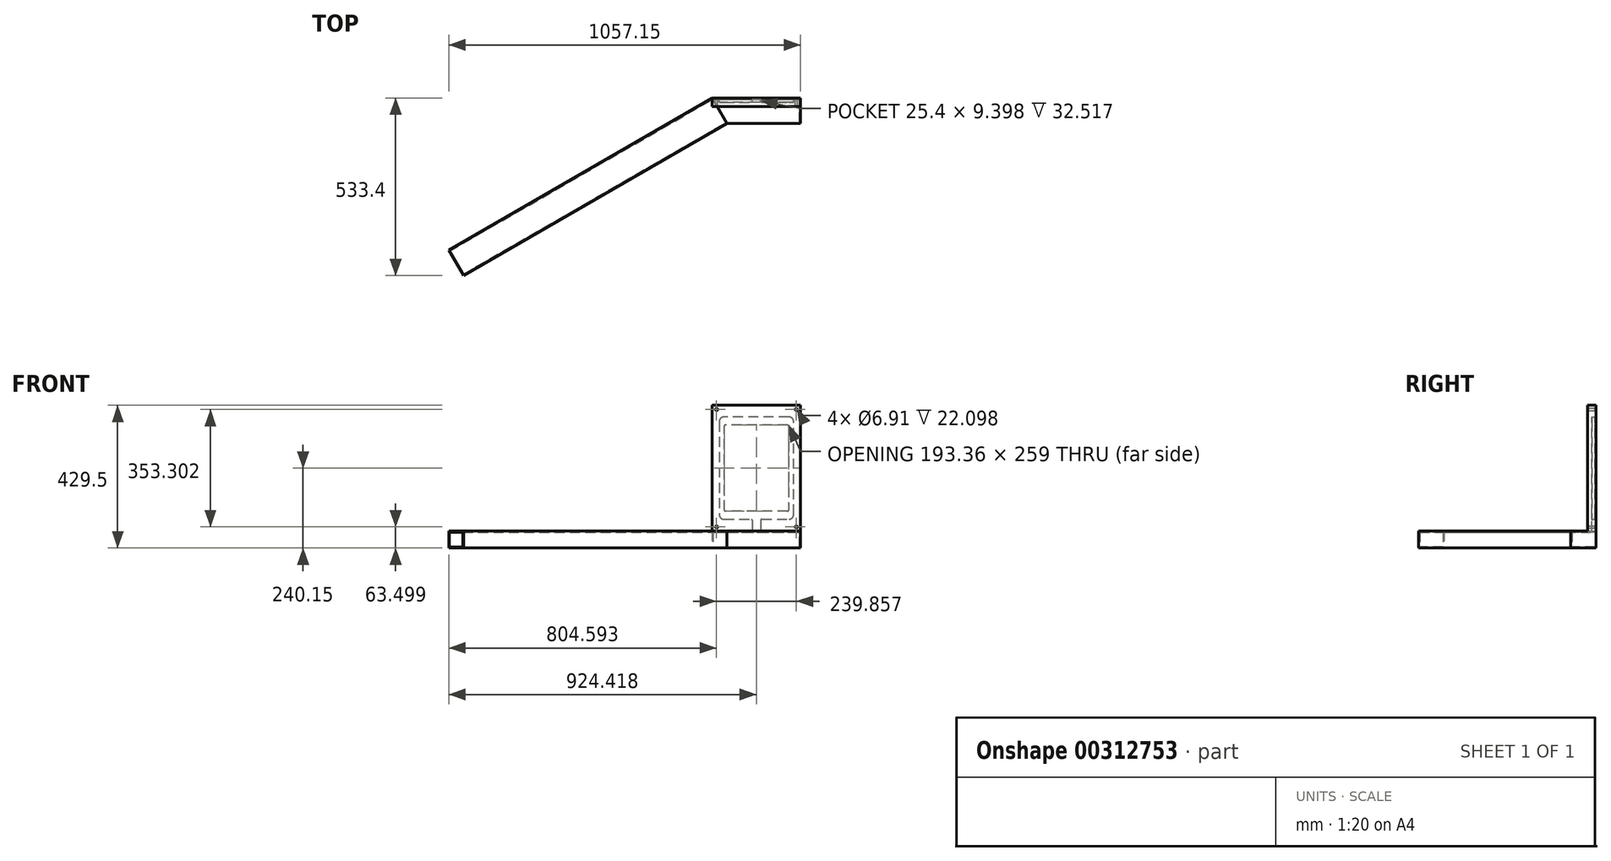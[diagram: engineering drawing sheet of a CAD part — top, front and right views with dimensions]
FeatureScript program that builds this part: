
annotation { "Feature Type Name" : "Feature", "Feature Type Description" : "" }
export const myFeature = defineFeature(function(context is Context, id is Id, definition is map)
    precondition{}
    {
        {
            var Q0;
            Q0=qCreatedBy(makeId("Front.planeOp"),FACE);
            var sketch = newSketch(context, id + "F0", { "sketchPlane" : qUnion([Q0])});
            skLineSegment(sketch, "E0", {"start": v(-259.8, 139.98) * mm, "end": v(-259.82, -139.5) * mm});
            skArc(sketch, "E1", {"start": v(-259.82, -139.5) * mm, "mid": v(-255.63, -149.6) * mm, "end": v(-245.53, -153.79) * mm});
            skLineSegment(sketch, "E2", {"start": v(-245.53, -153.79) * mm, "end": v(-163.8, -153.79) * mm});
            skArc(sketch, "E3", {"start": v(-160.76, -156.83) * mm, "mid": v(-161.65, -154.68) * mm, "end": v(-163.8, -153.79) * mm});
            skLineSegment(sketch, "E4", {"start": v(-160.76, -156.83) * mm, "end": v(-160.76, -171.77) * mm});
            skArc(sketch, "E5", {"start": v(-132.3, -153.79) * mm, "mid": v(-134.46, -154.68) * mm, "end": v(-135.36, -156.83) * mm});
            skLineSegment(sketch, "E6", {"start": v(-132.3, -153.79) * mm, "end": v(-50.58, -153.79) * mm});
            skArc(sketch, "E7", {"start": v(-50.58, -153.79) * mm, "mid": v(-40.48, -149.6) * mm, "end": v(-36.3, -139.5) * mm});
            skLineSegment(sketch, "E8", {"start": v(-36.3, -139.5) * mm, "end": v(-36.29, 139.97) * mm});
            skArc(sketch, "E9", {"start": v(-36.29, 139.97) * mm, "mid": v(-40.47, 150.08) * mm, "end": v(-50.58, 154.26) * mm});
            skLineSegment(sketch, "E10", {"start": v(-50.58, 154.26) * mm, "end": v(-245.52, 154.26) * mm});
            skArc(sketch, "E11", {"start": v(-245.52, 154.26) * mm, "mid": v(-255.63, 150.08) * mm, "end": v(-259.8, 139.98) * mm});
            skLineSegment(sketch, "E12", {"start": v(-244.82, -126.32) * mm, "end": v(-244.82, 126.32) * mm});
            skLineSegment(sketch, "E13", {"start": v(-54.64, -129.5) * mm, "end": v(-241.65, -129.5) * mm});
            skArc(sketch, "E14", {"start": v(-241.65, 129.5) * mm, "mid": v(-243.9, 128.57) * mm, "end": v(-244.82, 126.32) * mm});
            skArc(sketch, "E15", {"start": v(-51.46, 126.32) * mm, "mid": v(-52.4, 128.57) * mm, "end": v(-54.64, 129.5) * mm});
            skArc(sketch, "E16", {"start": v(-244.82, -126.32) * mm, "mid": v(-243.9, -128.57) * mm, "end": v(-241.65, -129.5) * mm});
            skArc(sketch, "E17", {"start": v(-54.64, -129.5) * mm, "mid": v(-52.4, -128.57) * mm, "end": v(-51.46, -126.32) * mm});
            skLineSegment(sketch, "E18", {"start": v(-135.36, -171.77) * mm, "end": v(-135.36, -156.83) * mm});
            skLineSegment(sketch, "E19", {"start": v(-160.76, -171.77) * mm, "end": v(-160.76, -187.92) * mm});
            skLineSegment(sketch, "E20", {"start": v(-135.36, -171.77) * mm, "end": v(-135.36, -187.92) * mm});
            skLineSegment(sketch, "E21", {"start": v(-160.76, -187.92) * mm, "end": v(-160.76, -189.35) * mm});
            skLineSegment(sketch, "E22", {"start": v(-135.36, -187.92) * mm, "end": v(-135.36, -189.35) * mm});
            skLineSegment(sketch, "E23", {"start": v(-15.41, -189.35) * mm, "end": v(-15.41, 189.35) * mm});
            skLineSegment(sketch, "E24", {"start": v(-280.67, -189.35) * mm, "end": v(-280.67, 189.35) * mm});
            skLineSegment(sketch, "E25", {"start": v(-15.41, 189.35) * mm, "end": v(-280.67, 189.35) * mm});
            skLineSegment(sketch, "E26", {"start": v(-280.67, -189.35) * mm, "end": v(-15.41, -189.35) * mm});
            skArc(sketch, "E27", {"start": v(-264.51, -176.65) * mm, "mid": v(-267.97, -173.2) * mm, "end": v(-271.42, -176.65) * mm});
            skArc(sketch, "E28", {"start": v(-271.42, -176.65) * mm, "mid": v(-267.97, -180.1) * mm, "end": v(-264.51, -176.65) * mm});
            skArc(sketch, "E29", {"start": v(-24.66, -176.65) * mm, "mid": v(-28.11, -173.2) * mm, "end": v(-31.56, -176.65) * mm});
            skArc(sketch, "E30", {"start": v(-31.56, -176.65) * mm, "mid": v(-28.11, -180.1) * mm, "end": v(-24.66, -176.65) * mm});
            skArc(sketch, "E31", {"start": v(-24.66, 176.65) * mm, "mid": v(-28.11, 180.1) * mm, "end": v(-31.56, 176.65) * mm});
            skArc(sketch, "E32", {"start": v(-31.56, 176.65) * mm, "mid": v(-28.11, 173.2) * mm, "end": v(-24.66, 176.65) * mm});
            skArc(sketch, "E33", {"start": v(-264.51, 176.65) * mm, "mid": v(-267.97, 180.1) * mm, "end": v(-271.42, 176.65) * mm});
            skArc(sketch, "E34", {"start": v(-271.42, 176.65) * mm, "mid": v(-267.97, 173.2) * mm, "end": v(-264.51, 176.65) * mm});
            skLineSegment(sketch, "E35", {"start": v(-54.64, 129.5) * mm, "end": v(-241.65, 129.5) * mm});
            skLineSegment(sketch, "E36", {"start": v(-51.46, 126.32) * mm, "end": v(-51.46, -126.32) * mm});
            skLineSegment(sketch, "E37", {"start": v(280.67, -189.35) * mm, "end": v(280.67, 189.35) * mm});
            skLineSegment(sketch, "E38", {"start": v(15.41, -189.35) * mm, "end": v(15.41, 189.35) * mm});
            skLineSegment(sketch, "E39", {"start": v(280.67, 189.35) * mm, "end": v(15.41, 189.35) * mm});
            skLineSegment(sketch, "E40", {"start": v(15.41, -189.35) * mm, "end": v(280.67, -189.35) * mm});
            skArc(sketch, "E41", {"start": v(31.56, -176.65) * mm, "mid": v(28.11, -173.2) * mm, "end": v(24.66, -176.65) * mm});
            skArc(sketch, "E42", {"start": v(24.66, -176.65) * mm, "mid": v(28.11, -180.1) * mm, "end": v(31.56, -176.65) * mm});
            skArc(sketch, "E43", {"start": v(271.42, -176.65) * mm, "mid": v(267.97, -173.2) * mm, "end": v(264.51, -176.65) * mm});
            skArc(sketch, "E44", {"start": v(264.51, -176.65) * mm, "mid": v(267.97, -180.1) * mm, "end": v(271.42, -176.65) * mm});
            skArc(sketch, "E45", {"start": v(271.42, 176.65) * mm, "mid": v(267.97, 180.1) * mm, "end": v(264.51, 176.65) * mm});
            skArc(sketch, "E46", {"start": v(264.51, 176.65) * mm, "mid": v(267.97, 173.2) * mm, "end": v(271.42, 176.65) * mm});
            skArc(sketch, "E47", {"start": v(31.56, 176.65) * mm, "mid": v(28.11, 180.1) * mm, "end": v(24.66, 176.65) * mm});
            skArc(sketch, "E48", {"start": v(24.66, 176.65) * mm, "mid": v(28.11, 173.2) * mm, "end": v(31.56, 176.65) * mm});
            skSolve(sketch);
        }
        {
            var Q0;
            Q0=makeQuery(id+"F0.imprint","IMPRINT",FACE,{"disambiguationData":[TD([[makeQuery(id+"F0.imprint","IMPRINT",EDGE,{"derivedFrom":sQuery(id+"F0.wireOp",EDGE,"E37")}),1.0]])]});
            var Q1;
            Q1=makeQuery(id+"F0.imprint","IMPRINT",FACE,{"disambiguationData":[TD([[makeQuery(id+"F0.imprint","IMPRINT",EDGE,{"derivedFrom":sQuery(id+"F0.wireOp",EDGE,"E0")}),-1.0]])]});
            extrude(context, id + "F1", {"entities" : qUnion([Q0, Q1]), "depth" : 12.7 * mm});
        }
        {
            var Q0;
            Q0=makeQuery(id+"F0.imprint","IMPRINT",FACE,{"disambiguationData":[TD([[makeQuery(id+"F0.imprint","IMPRINT",EDGE,{"derivedFrom":sQuery(id+"F0.wireOp",EDGE,"E0")}),1.0]])]});
            var Q1;
            Q1=makeQuery(id+"F0.imprint","IMPRINT",FACE,{"disambiguationData":[TD([[makeQuery(id+"F0.imprint","IMPRINT",EDGE,{"derivedFrom":sQuery(id+"F0.wireOp",EDGE,"E31")}),1.0]])]});
            var Q2;
            Q2=makeQuery(id+"F0.imprint","IMPRINT",FACE,{"disambiguationData":[TD([[makeQuery(id+"F0.imprint","IMPRINT",EDGE,{"derivedFrom":sQuery(id+"F0.wireOp",EDGE,"E29")}),1.0]])]});
            var Q3;
            Q3=makeQuery(id+"F0.imprint","IMPRINT",FACE,{"disambiguationData":[TD([[makeQuery(id+"F0.imprint","IMPRINT",EDGE,{"derivedFrom":sQuery(id+"F0.wireOp",EDGE,"E27")}),1.0]])]});
            var Q4;
            Q4=makeQuery(id+"F0.imprint","IMPRINT",FACE,{"disambiguationData":[TD([[makeQuery(id+"F0.imprint","IMPRINT",EDGE,{"derivedFrom":sQuery(id+"F0.wireOp",EDGE,"E33")}),1.0]])]});
            extrude(context, id + "F2", {"entities" : qUnion([Q0, Q1, Q2, Q3, Q4]), "operationType" : NewBodyOperationType.ADD, "depth" : 3.3 * mm});
        }
        {
            var Q0;
            Q0=makeQuery(id+"F1.opExtrude","SWEPT_FACE",FACE,{"disambiguationData":[OSD([sQuery(id+"F0.wireOp",EDGE,"E23")])]});
            var sketch = newSketch(context, id + "F3", { "sketchPlane" : qUnion([Q0])});
            skLineSegment(sketch, "E49.bottom", {"start": v(0, -189.35) * mm, "end": v(-76.2, -189.35) * mm});
            skLineSegment(sketch, "E49.top", {"start": v(0, -240.15) * mm, "end": v(-76.2, -240.15) * mm});
            skLineSegment(sketch, "E49.left", {"start": v(0, -189.35) * mm, "end": v(0, -240.15) * mm});
            skLineSegment(sketch, "E49.right", {"start": v(-76.2, -189.35) * mm, "end": v(-76.2, -240.15) * mm});
            skLineSegment(sketch, "E50.0", {"start": v(-3.17, -236.98) * mm, "end": v(-73.02, -236.98) * mm});
            skLineSegment(sketch, "E50.1", {"start": v(-3.18, -192.53) * mm, "end": v(-3.17, -236.98) * mm});
            skLineSegment(sketch, "E50.2", {"start": v(-3.18, -192.53) * mm, "end": v(-73.02, -192.53) * mm});
            skLineSegment(sketch, "E50.3", {"start": v(-73.02, -192.53) * mm, "end": v(-73.02, -236.98) * mm});
            skSolve(sketch);
        }
        {
            var Q0;
            Q0 = qSketchRegion(id + "F3", true);
            var Q1;
            Q1=makeQuery(id+"F1.opExtrude","SWEPT_FACE",FACE,{"disambiguationData":[OSD([sQuery(id+"F0.wireOp",EDGE,"E24")])]});
            extrude(context, id + "F4", {"entities" : qUnion([Q0]), "endBound" : BoundingType.UP_TO_SURFACE, "oppositeDirection" : true, "endBoundEntityFace" : qUnion([Q1]), "depth" : 275.59 * mm});
        }
        {
            var Q0;
            Q0=makeQuery(id+"F4.opExtrude","SWEPT_FACE",FACE,{"disambiguationData":[OSD([sQuery(id+"F3.wireOp",EDGE,"E49.top")])]});
            var sketch = newSketch(context, id + "F5", { "sketchPlane" : qUnion([Q0])});
            skLineSegment(sketch, "E51", {"start": v(-280.67, 0) * mm, "end": v(-280.67, 76.2) * mm});
            skLineSegment(sketch, "E52", {"start": v(-280.67, 76.2) * mm, "end": v(-236.67, 76.2) * mm});
            skLineSegment(sketch, "E53", {"start": v(-236.67, 76.2) * mm, "end": v(-280.67, 0) * mm});
            skSolve(sketch);
        }
        {
            var Q0;
            Q0=makeQuery(id+"F5.imprint","IMPRINT",FACE,{"disambiguationData":[TD([[makeQuery(id+"F5.imprint","IMPRINT",EDGE,{"derivedFrom":sQuery(id+"F5.wireOp",EDGE,"E51")}),-1.0]])]});
            extrude(context, id + "F6", {"entities" : qUnion([Q0]), "operationType" : NewBodyOperationType.REMOVE, "oppositeDirection" : true, "depth" : 50.8 * mm});
        }
        {
            var Q0;
            Q0=makeQuery(id+"F6.boolean.opBoolean","COPY",FACE,{"derivedFrom":makeQuery(id+"F6.opExtrude","SWEPT_FACE",FACE,{"disambiguationData":[OSD([sQuery(id+"F5.wireOp",EDGE,"E53")])]})});
            extrude(context, id + "F7", {"entities" : qUnion([Q0]), "depth" : 914.4 * mm});
        }
        {
            var Q0;
            Q0=makeQuery(id+"F1.opExtrude","CAP_FACE",FACE,{"disambiguationData":[OSD([sQuery(id+"F0.wireOp",EDGE,"E0"),sQuery(id+"F0.wireOp",EDGE,"E1"),sQuery(id+"F0.wireOp",EDGE,"E2"),sQuery(id+"F0.wireOp",EDGE,"E3"),sQuery(id+"F0.wireOp",EDGE,"E4"),sQuery(id+"F0.wireOp",EDGE,"E5"),sQuery(id+"F0.wireOp",EDGE,"E6"),sQuery(id+"F0.wireOp",EDGE,"E7"),sQuery(id+"F0.wireOp",EDGE,"E8"),sQuery(id+"F0.wireOp",EDGE,"E9"),sQuery(id+"F0.wireOp",EDGE,"E10"),sQuery(id+"F0.wireOp",EDGE,"E11"),sQuery(id+"F0.wireOp",EDGE,"E18"),sQuery(id+"F0.wireOp",EDGE,"E19"),sQuery(id+"F0.wireOp",EDGE,"E20"),sQuery(id+"F0.wireOp",EDGE,"E21"),sQuery(id+"F0.wireOp",EDGE,"E22"),sQuery(id+"F0.wireOp",EDGE,"E23"),sQuery(id+"F0.wireOp",EDGE,"E24"),sQuery(id+"F0.wireOp",EDGE,"E25"),sQuery(id+"F0.wireOp",EDGE,"E26"),sQuery(id+"F0.wireOp",EDGE,"E27"),sQuery(id+"F0.wireOp",EDGE,"E28"),sQuery(id+"F0.wireOp",EDGE,"E29"),sQuery(id+"F0.wireOp",EDGE,"E30"),sQuery(id+"F0.wireOp",EDGE,"E31"),sQuery(id+"F0.wireOp",EDGE,"E32"),sQuery(id+"F0.wireOp",EDGE,"E33"),sQuery(id+"F0.wireOp",EDGE,"E34")])],"isStart":false});
            var sketch = newSketch(context, id + "F8", { "sketchPlane" : qUnion([Q0])});
            skLineSegment(sketch, "E54.bottom", {"start": v(-15.41, 189.35) * mm, "end": v(-280.67, 189.35) * mm});
            skLineSegment(sketch, "E54.top", {"start": v(-15.41, -189.35) * mm, "end": v(-280.67, -189.35) * mm});
            skLineSegment(sketch, "E54.left", {"start": v(-15.41, 189.35) * mm, "end": v(-15.41, -189.35) * mm});
            skLineSegment(sketch, "E54.right", {"start": v(-280.67, 189.35) * mm, "end": v(-280.67, -189.35) * mm});
            skCircle(sketch, "E55", {"center": v(-267.97, 176.65) * mm, "radius": 3.45 * mm});
            skPoint(sketch, "E55.first.point", {"position": v(-265.03, 178.47) * mm});
            skPoint(sketch, "E55.second.point", {"position": v(-270.75, 174.6) * mm});
            skPoint(sketch, "E55.third.point", {"position": v(-271.4, 176.96) * mm});
            skCircle(sketch, "E56", {"center": v(-28.11, 176.65) * mm, "radius": 3.45 * mm});
            skPoint(sketch, "E56.first.point", {"position": v(-24.66, 176.4) * mm});
            skPoint(sketch, "E56.second.point", {"position": v(-31.5, 177.3) * mm});
            skPoint(sketch, "E56.third.point", {"position": v(-29.76, 173.62) * mm});
            skCircle(sketch, "E57", {"center": v(-28.11, -176.65) * mm, "radius": 3.45 * mm});
            skPoint(sketch, "E57.first.point", {"position": v(-27.3, -173.3) * mm});
            skPoint(sketch, "E57.second.point", {"position": v(-29.34, -179.88) * mm});
            skPoint(sketch, "E57.third.point", {"position": v(-24.9, -177.9) * mm});
            skCircle(sketch, "E58", {"center": v(-267.97, -176.65) * mm, "radius": 3.45 * mm});
            skPoint(sketch, "E58.first.point", {"position": v(-264.61, -177.47) * mm});
            skPoint(sketch, "E58.second.point", {"position": v(-270.08, -173.92) * mm});
            skPoint(sketch, "E58.third.point", {"position": v(-269.94, -179.49) * mm});
            skSolve(sketch);
        }
        {
            var Q0;
            Q0 = qSketchRegion(id + "F8", true);
            extrude(context, id + "F9", {"entities" : qUnion([Q0]), "depth" : 12.7 * mm});
        }
        {
            var Q0;
            Q0=makeQuery(id+"F9.opExtrude","SWEPT_BODY",BODY,{"disambiguationData":[OSD([sQuery(id+"F8.wireOp",EDGE,"E54.bottom"),sQuery(id+"F8.wireOp",EDGE,"E54.top"),sQuery(id+"F8.wireOp",EDGE,"E54.left"),sQuery(id+"F8.wireOp",EDGE,"E54.right"),sQuery(id+"F8.wireOp",EDGE,"E55"),sQuery(id+"F8.wireOp",EDGE,"E56"),sQuery(id+"F8.wireOp",EDGE,"E57"),sQuery(id+"F8.wireOp",EDGE,"E58")])]});
            var Q1;
            Q1=makeQuery(id+"F4.opExtrude","SWEPT_BODY",BODY,{"disambiguationData":[OSD([sQuery(id+"F3.wireOp",EDGE,"E49.bottom"),sQuery(id+"F3.wireOp",EDGE,"E49.top"),sQuery(id+"F3.wireOp",EDGE,"E49.left"),sQuery(id+"F3.wireOp",EDGE,"E49.right"),sQuery(id+"F3.wireOp",EDGE,"E50.0"),sQuery(id+"F3.wireOp",EDGE,"E50.1"),sQuery(id+"F3.wireOp",EDGE,"E50.2"),sQuery(id+"F3.wireOp",EDGE,"E50.3")])]});
            booleanBodies(context, id + "F10", {"operationType" : BooleanOperationType.UNION, "tools" : qUnion([Q0, Q1])});
        }
        {
            var Q0;
            Q0=makeQuery(id+"F10.opBoolean","MERGE",FACE,{"derivedFrom":[makeQuery(id+"F4.opExtrude","CAP_FACE",FACE,{"disambiguationData":[OSD([sQuery(id+"F3.wireOp",EDGE,"E49.bottom"),sQuery(id+"F3.wireOp",EDGE,"E49.top"),sQuery(id+"F3.wireOp",EDGE,"E49.left"),sQuery(id+"F3.wireOp",EDGE,"E49.right"),sQuery(id+"F3.wireOp",EDGE,"E50.0"),sQuery(id+"F3.wireOp",EDGE,"E50.1"),sQuery(id+"F3.wireOp",EDGE,"E50.2"),sQuery(id+"F3.wireOp",EDGE,"E50.3")])],"isStart":true}),makeQuery(id+"F9.opExtrude","SWEPT_FACE",FACE,{"disambiguationData":[OSD([sQuery(id+"F8.wireOp",EDGE,"E54.left")])]})]});
            var sketch = newSketch(context, id + "F11", { "sketchPlane" : qUnion([Q0])});
            skLineSegment(sketch, "E59.bottom", {"start": v(0, -240.15) * mm, "end": v(-76.2, -240.15) * mm});
            skLineSegment(sketch, "E59.top", {"start": v(0, -189.35) * mm, "end": v(-76.2, -189.35) * mm});
            skLineSegment(sketch, "E59.left", {"start": v(0, -240.15) * mm, "end": v(0, -189.35) * mm});
            skLineSegment(sketch, "E59.right", {"start": v(-76.2, -240.15) * mm, "end": v(-76.2, -189.35) * mm});
            skSolve(sketch);
        }
        {
            var Q0;
            Q0 = qSketchRegion(id + "F11", true);
            extrude(context, id + "F12", {"entities" : qUnion([Q0]), "operationType" : NewBodyOperationType.ADD, "oppositeDirection" : true, "depth" : 3.17 * mm});
        }
        {
            var Q0;
            Q0=makeQuery(id+"F1.opExtrude","SWEPT_BODY",BODY,{"disambiguationData":[OSD([sQuery(id+"F0.wireOp",EDGE,"E37"),sQuery(id+"F0.wireOp",EDGE,"E38"),sQuery(id+"F0.wireOp",EDGE,"E39"),sQuery(id+"F0.wireOp",EDGE,"E40"),sQuery(id+"F0.wireOp",EDGE,"E41"),sQuery(id+"F0.wireOp",EDGE,"E42"),sQuery(id+"F0.wireOp",EDGE,"E43"),sQuery(id+"F0.wireOp",EDGE,"E44"),sQuery(id+"F0.wireOp",EDGE,"E45"),sQuery(id+"F0.wireOp",EDGE,"E46"),sQuery(id+"F0.wireOp",EDGE,"E47"),sQuery(id+"F0.wireOp",EDGE,"E48")])]});
            deleteBodies(context, id + "F13", {"entities" : qUnion([Q0])});
        }
    });
